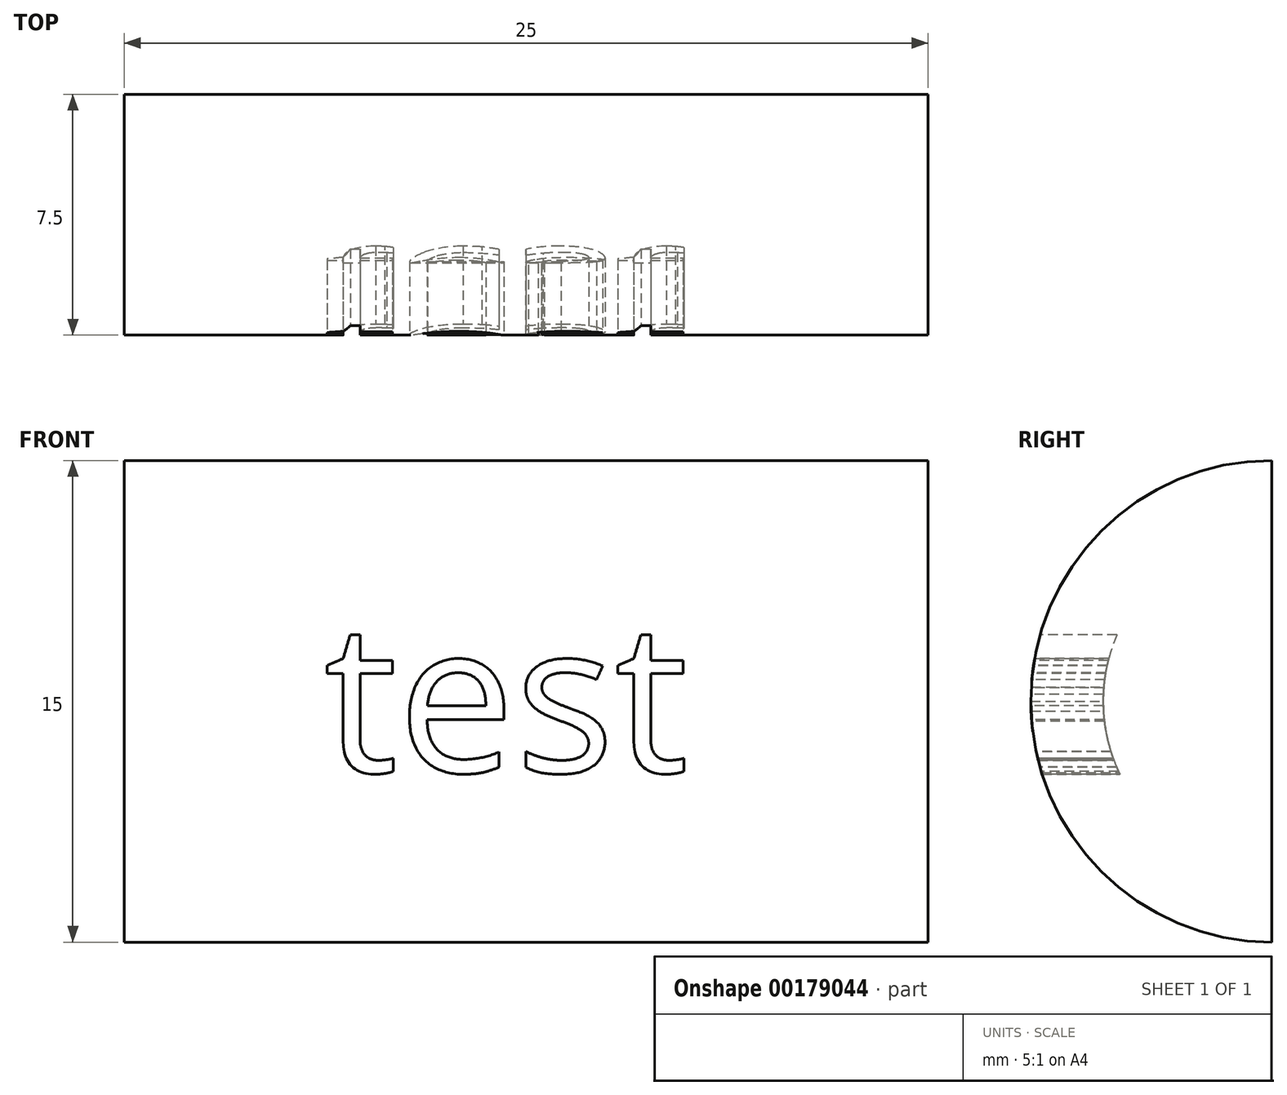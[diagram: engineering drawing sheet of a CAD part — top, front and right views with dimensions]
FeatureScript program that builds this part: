
annotation { "Feature Type Name" : "Feature", "Feature Type Description" : "" }
export const myFeature = defineFeature(function(context is Context, id is Id, definition is map)
    precondition{}
    {
        {
            var Q0;
            Q0=qCreatedBy(makeId("Right.planeOp"),FACE);
            var sketch = newSketch(context, id + "F0", { "sketchPlane" : qUnion([Q0])});
            skArc(sketch, "E0", {"start": v(0, 7.5) * mm, "mid": v(-7.5, 0) * mm, "end": v(0, -7.5) * mm});
            skLineSegment(sketch, "E1", {"start": v(0, 7.5) * mm, "end": v(0, -7.5) * mm});
            skSolve(sketch);
        }
        {
            var Q0;
            Q0 = qSketchRegion(id + "F0", true);
            extrude(context, id + "F1", {"entities" : qUnion([Q0]), "depth" : 25 * mm});
        }
        {
            var Q0;
            Q0=qCreatedBy(makeId("Front.planeOp"),FACE);
            cPlane(context, id + "F2", {"entities" : qUnion([Q0]), "cplaneType" : CPlaneType.OFFSET, "offset" : 25 * mm, "width" : 150 * mm, "height" : 150 * mm});
        }
        {
            var Q0;
            Q0=qCreatedBy(id+"F2.planeOp",FACE);
            var sketch = newSketch(context, id + "F3", { "sketchPlane" : qUnion([Q0])});
            skText(sketch, "E2", { "text": "test", "fontName": "OpenSans-Regular.ttf"});
            const initialGuessF3  = {"E2": [0.00621, -0.00221, 1, 0, 0.00468]};
            skSetInitialGuess(sketch, initialGuessF3);
            skSolve(sketch);
        }
        {
            var Q0;
            Q0=makeQuery(id+"F1.opExtrude","CAP_FACE",FACE,{"disambiguationData":[OSD([sQuery(id+"F0.wireOp",EDGE,"E0"),sQuery(id+"F0.wireOp",EDGE,"E1")])],"isStart":true});
            var sketch = newSketch(context, id + "F4", { "sketchPlane" : qUnion([Q0])});
            skArc(sketch, "E3.0", {"start": v(0, 7.5) * mm, "mid": v(7.5, 0) * mm, "end": v(0, -7.5) * mm});
            skArc(sketch, "E4", {"start": v(0, 5.25) * mm, "mid": v(5.25, 0) * mm, "end": v(0, -5.25) * mm});
            skSolve(sketch);
        }
        {
            var Q0;
            Q0 = qSketchRegion(id + "F4", true);
            var Q1;
            Q1=sQuery(id+"F4.wireOp",EDGE,"E4");
            var Q2;
            Q2=makeQuery(id+"F1.opExtrude","CAP_FACE",FACE,{"disambiguationData":[OSD([sQuery(id+"F0.wireOp",EDGE,"E0"),sQuery(id+"F0.wireOp",EDGE,"E1")])],"isStart":false});
            extrude(context, id + "F5", {"entities" : qUnion([Q0]), "bodyType" : ToolBodyType.SURFACE, "surfaceEntities" : qUnion([Q1]), "endBound" : BoundingType.UP_TO_SURFACE, "oppositeDirection" : true, "endBoundEntityFace" : qUnion([Q2]), "depth" : 25 * mm});
        }
        {
            var Q0;
            Q0 = qSketchRegion(id + "F3", true);
            var Q1;
            Q1=makeQuery(id+"F5.opExtrude","SWEPT_FACE",FACE,{"disambiguationData":[OSD([sQuery(id+"F4.wireOp",EDGE,"E4")])]});
            extrude(context, id + "F6", {"entities" : qUnion([Q0]), "endBound" : BoundingType.UP_TO_SURFACE, "oppositeDirection" : true, "endBoundEntityFace" : qUnion([Q1]), "depth" : 25 * mm});
        }
        {
            var Q0;
            Q0=makeQuery(id+"F6.opExtrude","SWEPT_BODY",BODY,{"disambiguationData":[OSD([sQuery(id+"F3.wireOp",EDGE,"E2.sketch_text.stroke-63"),sQuery(id+"F3.wireOp",EDGE,"E2.sketch_text.stroke-64"),sQuery(id+"F3.wireOp",EDGE,"E2.sketch_text.stroke-65"),sQuery(id+"F3.wireOp",EDGE,"E2.sketch_text.stroke-66"),sQuery(id+"F3.wireOp",EDGE,"E2.sketch_text.stroke-67"),sQuery(id+"F3.wireOp",EDGE,"E2.sketch_text.stroke-68"),sQuery(id+"F3.wireOp",EDGE,"E2.sketch_text.stroke-69"),sQuery(id+"F3.wireOp",EDGE,"E2.sketch_text.stroke-70"),sQuery(id+"F3.wireOp",EDGE,"E2.sketch_text.stroke-71"),sQuery(id+"F3.wireOp",EDGE,"E2.sketch_text.stroke-72"),sQuery(id+"F3.wireOp",EDGE,"E2.sketch_text.stroke-73"),sQuery(id+"F3.wireOp",EDGE,"E2.sketch_text.stroke-74"),sQuery(id+"F3.wireOp",EDGE,"E2.sketch_text.stroke-75"),sQuery(id+"F3.wireOp",EDGE,"E2.sketch_text.stroke-76"),sQuery(id+"F3.wireOp",EDGE,"E2.sketch_text.stroke-77"),sQuery(id+"F3.wireOp",EDGE,"E2.sketch_text.stroke-78"),sQuery(id+"F3.wireOp",EDGE,"E2.sketch_text.stroke-79"),sQuery(id+"F3.wireOp",EDGE,"E2.sketch_text.stroke-80"),sQuery(id+"F3.wireOp",EDGE,"E2.sketch_text.stroke-81")])]});
            var Q1;
            Q1=makeQuery(id+"F6.opExtrude","SWEPT_BODY",BODY,{"disambiguationData":[OSD([sQuery(id+"F3.wireOp",EDGE,"E2.sketch_text.stroke-38"),sQuery(id+"F3.wireOp",EDGE,"E2.sketch_text.stroke-39"),sQuery(id+"F3.wireOp",EDGE,"E2.sketch_text.stroke-40"),sQuery(id+"F3.wireOp",EDGE,"E2.sketch_text.stroke-41"),sQuery(id+"F3.wireOp",EDGE,"E2.sketch_text.stroke-42"),sQuery(id+"F3.wireOp",EDGE,"E2.sketch_text.stroke-43"),sQuery(id+"F3.wireOp",EDGE,"E2.sketch_text.stroke-44"),sQuery(id+"F3.wireOp",EDGE,"E2.sketch_text.stroke-45"),sQuery(id+"F3.wireOp",EDGE,"E2.sketch_text.stroke-46"),sQuery(id+"F3.wireOp",EDGE,"E2.sketch_text.stroke-47"),sQuery(id+"F3.wireOp",EDGE,"E2.sketch_text.stroke-48"),sQuery(id+"F3.wireOp",EDGE,"E2.sketch_text.stroke-49"),sQuery(id+"F3.wireOp",EDGE,"E2.sketch_text.stroke-50"),sQuery(id+"F3.wireOp",EDGE,"E2.sketch_text.stroke-51"),sQuery(id+"F3.wireOp",EDGE,"E2.sketch_text.stroke-52"),sQuery(id+"F3.wireOp",EDGE,"E2.sketch_text.stroke-53"),sQuery(id+"F3.wireOp",EDGE,"E2.sketch_text.stroke-54"),sQuery(id+"F3.wireOp",EDGE,"E2.sketch_text.stroke-55"),sQuery(id+"F3.wireOp",EDGE,"E2.sketch_text.stroke-56"),sQuery(id+"F3.wireOp",EDGE,"E2.sketch_text.stroke-57"),sQuery(id+"F3.wireOp",EDGE,"E2.sketch_text.stroke-58"),sQuery(id+"F3.wireOp",EDGE,"E2.sketch_text.stroke-59"),sQuery(id+"F3.wireOp",EDGE,"E2.sketch_text.stroke-60"),sQuery(id+"F3.wireOp",EDGE,"E2.sketch_text.stroke-61"),sQuery(id+"F3.wireOp",EDGE,"E2.sketch_text.stroke-62")])]});
            var Q2;
            Q2=makeQuery(id+"F6.opExtrude","SWEPT_BODY",BODY,{"disambiguationData":[OSD([sQuery(id+"F3.wireOp",EDGE,"E2.sketch_text.stroke-19"),sQuery(id+"F3.wireOp",EDGE,"E2.sketch_text.stroke-20"),sQuery(id+"F3.wireOp",EDGE,"E2.sketch_text.stroke-21"),sQuery(id+"F3.wireOp",EDGE,"E2.sketch_text.stroke-22"),sQuery(id+"F3.wireOp",EDGE,"E2.sketch_text.stroke-23"),sQuery(id+"F3.wireOp",EDGE,"E2.sketch_text.stroke-24"),sQuery(id+"F3.wireOp",EDGE,"E2.sketch_text.stroke-25"),sQuery(id+"F3.wireOp",EDGE,"E2.sketch_text.stroke-26"),sQuery(id+"F3.wireOp",EDGE,"E2.sketch_text.stroke-27"),sQuery(id+"F3.wireOp",EDGE,"E2.sketch_text.stroke-28"),sQuery(id+"F3.wireOp",EDGE,"E2.sketch_text.stroke-29"),sQuery(id+"F3.wireOp",EDGE,"E2.sketch_text.stroke-30"),sQuery(id+"F3.wireOp",EDGE,"E2.sketch_text.stroke-31"),sQuery(id+"F3.wireOp",EDGE,"E2.sketch_text.stroke-32"),sQuery(id+"F3.wireOp",EDGE,"E2.sketch_text.stroke-33"),sQuery(id+"F3.wireOp",EDGE,"E2.sketch_text.stroke-34"),sQuery(id+"F3.wireOp",EDGE,"E2.sketch_text.stroke-35"),sQuery(id+"F3.wireOp",EDGE,"E2.sketch_text.stroke-36"),sQuery(id+"F3.wireOp",EDGE,"E2.sketch_text.stroke-37")])]});
            var Q3;
            Q3=makeQuery(id+"F6.opExtrude","SWEPT_BODY",BODY,{"disambiguationData":[OSD([sQuery(id+"F3.wireOp",EDGE,"E2.sketch_text.stroke-0"),sQuery(id+"F3.wireOp",EDGE,"E2.sketch_text.stroke-1"),sQuery(id+"F3.wireOp",EDGE,"E2.sketch_text.stroke-2"),sQuery(id+"F3.wireOp",EDGE,"E2.sketch_text.stroke-3"),sQuery(id+"F3.wireOp",EDGE,"E2.sketch_text.stroke-4"),sQuery(id+"F3.wireOp",EDGE,"E2.sketch_text.stroke-5"),sQuery(id+"F3.wireOp",EDGE,"E2.sketch_text.stroke-6"),sQuery(id+"F3.wireOp",EDGE,"E2.sketch_text.stroke-7"),sQuery(id+"F3.wireOp",EDGE,"E2.sketch_text.stroke-8"),sQuery(id+"F3.wireOp",EDGE,"E2.sketch_text.stroke-9"),sQuery(id+"F3.wireOp",EDGE,"E2.sketch_text.stroke-10"),sQuery(id+"F3.wireOp",EDGE,"E2.sketch_text.stroke-11"),sQuery(id+"F3.wireOp",EDGE,"E2.sketch_text.stroke-12"),sQuery(id+"F3.wireOp",EDGE,"E2.sketch_text.stroke-13"),sQuery(id+"F3.wireOp",EDGE,"E2.sketch_text.stroke-14"),sQuery(id+"F3.wireOp",EDGE,"E2.sketch_text.stroke-15"),sQuery(id+"F3.wireOp",EDGE,"E2.sketch_text.stroke-16"),sQuery(id+"F3.wireOp",EDGE,"E2.sketch_text.stroke-17"),sQuery(id+"F3.wireOp",EDGE,"E2.sketch_text.stroke-18")])]});
            var Q4;
            Q4=makeQuery(id+"F1.opExtrude","SWEPT_BODY",BODY,{"disambiguationData":[OSD([sQuery(id+"F0.wireOp",EDGE,"E0"),sQuery(id+"F0.wireOp",EDGE,"E1")])]});
            booleanBodies(context, id + "F7", {"operationType" : BooleanOperationType.SUBTRACTION, "tools" : qUnion([Q0, Q1, Q2, Q3]), "targets" : qUnion([Q4])});
        }
    });
